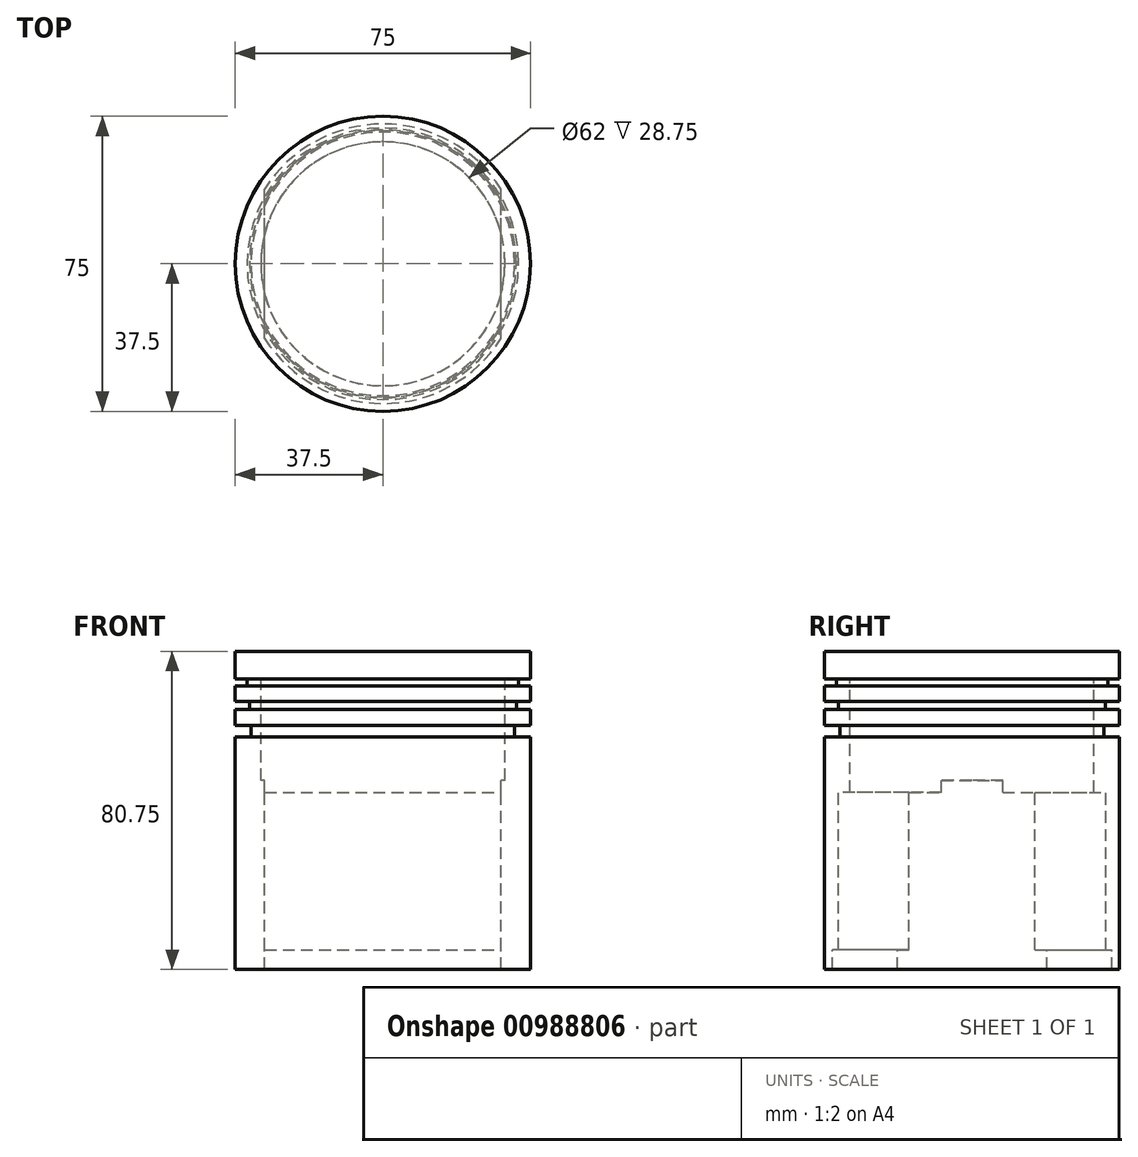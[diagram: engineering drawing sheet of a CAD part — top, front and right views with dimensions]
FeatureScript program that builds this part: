
annotation { "Feature Type Name" : "Feature", "Feature Type Description" : "" }
export const myFeature = defineFeature(function(context is Context, id is Id, definition is map)
    precondition{}
    {
        {
            var Q0;
            Q0=qCreatedBy(makeId("Right.planeOp"),FACE);
            var sketch = newSketch(context, id + "F0", { "sketchPlane" : qUnion([Q0])});
            skLineSegment(sketch, "E0", {"start": v(0, 0) * mm, "end": v(37.5, 0) * mm});
            skLineSegment(sketch, "E1", {"start": v(37.5, 0) * mm, "end": v(37.5, -7) * mm});
            skLineSegment(sketch, "E2", {"start": v(37.5, -7) * mm, "end": v(34.5, -7) * mm});
            skLineSegment(sketch, "E3", {"start": v(34.5, -7) * mm, "end": v(34.5, -8.75) * mm});
            skLineSegment(sketch, "E4", {"start": v(34.5, -8.75) * mm, "end": v(37.5, -8.75) * mm});
            skLineSegment(sketch, "E5", {"start": v(37.5, -8.75) * mm, "end": v(37.5, -12.75) * mm});
            skLineSegment(sketch, "E6", {"start": v(37.5, -12.75) * mm, "end": v(33.9, -12.75) * mm});
            skLineSegment(sketch, "E7", {"start": v(33.9, -12.75) * mm, "end": v(33.9, -14.75) * mm});
            skLineSegment(sketch, "E8", {"start": v(33.9, -14.75) * mm, "end": v(37.5, -14.75) * mm});
            skLineSegment(sketch, "E9", {"start": v(37.5, -14.75) * mm, "end": v(37.5, -18.75) * mm});
            skLineSegment(sketch, "E10", {"start": v(37.5, -18.75) * mm, "end": v(33.5, -18.75) * mm});
            skLineSegment(sketch, "E11", {"start": v(33.5, -18.75) * mm, "end": v(33.5, -21.75) * mm});
            skLineSegment(sketch, "E12", {"start": v(33.5, -21.75) * mm, "end": v(37.5, -21.75) * mm});
            skLineSegment(sketch, "E13", {"start": v(37.5, -21.75) * mm, "end": v(37.5, -80.75) * mm});
            skLineSegment(sketch, "E14", {"start": v(37.5, -80.75) * mm, "end": v(35.5, -80.75) * mm});
            skLineSegment(sketch, "E15", {"start": v(35.5, -80.75) * mm, "end": v(35.5, -75.75) * mm});
            skLineSegment(sketch, "E16", {"start": v(35.5, -75.75) * mm, "end": v(34, -75.75) * mm});
            skLineSegment(sketch, "E17", {"start": v(34, -75.75) * mm, "end": v(34, -35.75) * mm});
            skLineSegment(sketch, "E18", {"start": v(34, -35.75) * mm, "end": v(31, -35.75) * mm});
            skLineSegment(sketch, "E19", {"start": v(31, -35.75) * mm, "end": v(31, -7) * mm});
            skLineSegment(sketch, "E20", {"start": v(31, -7) * mm, "end": v(0, -7) * mm});
            skLineSegment(sketch, "E21", {"start": v(0, -7) * mm, "end": v(0, 0) * mm});
            skLineSegment(sketch, "E22", {"start": v(0, 0) * mm, "end": v(0, -42.55) * mm, "construction": true});
            skPoint(sketch, "E22.endSnap0", {"position": v(0, -3.5) * mm});
            skSolve(sketch);
        }
        {
            var Q0;
            Q0 = qSketchRegion(id + "F0", true);
            var Q1;
            Q1=sQuery(id+"F0.wireOp",EDGE,"E22");
            revolve(context, id + "F1", {"surfaceOperationType" : NewSurfaceOperationType.NEW, "entities" : qUnion([Q0]), "axis" : qUnion([Q1]), "revolveType" : RevolveType.FULL});
        }
        {
            var Q0;
            Q0=makeQuery(id+"F1.opRevolve","SWEPT_FACE",FACE,{"disambiguationData":[OSD([sQuery(id+"F0.wireOp",EDGE,"E14")])]});
            var sketch = newSketch(context, id + "F2", { "sketchPlane" : qUnion([Q0])});
            skArc(sketch, "E23.0", {"start": v(-30, 22.5) * mm, "mid": v(-37.5, 0) * mm, "end": v(-30, -22.5) * mm});
            skLineSegment(sketch, "E24", {"start": v(-30, 22.5) * mm, "end": v(-30, -22.5) * mm});
            skLineSegment(sketch, "E25", {"start": v(30, 22.5) * mm, "end": v(30, -22.5) * mm});
            skArc(sketch, "E26.trimOffspring", {"start": v(30, -22.5) * mm, "mid": v(37.5, 0) * mm, "end": v(30, 22.5) * mm});
            skSolve(sketch);
        }
        {
            var Q0;
            Q0 = qSketchRegion(id + "F2", true);
            extrude(context, id + "F3", {"entities" : qUnion([Q0]), "operationType" : NewBodyOperationType.ADD, "oppositeDirection" : true, "depth" : 48 * mm, "offsetDistance" : 25.4 * mm});
        }
    });
